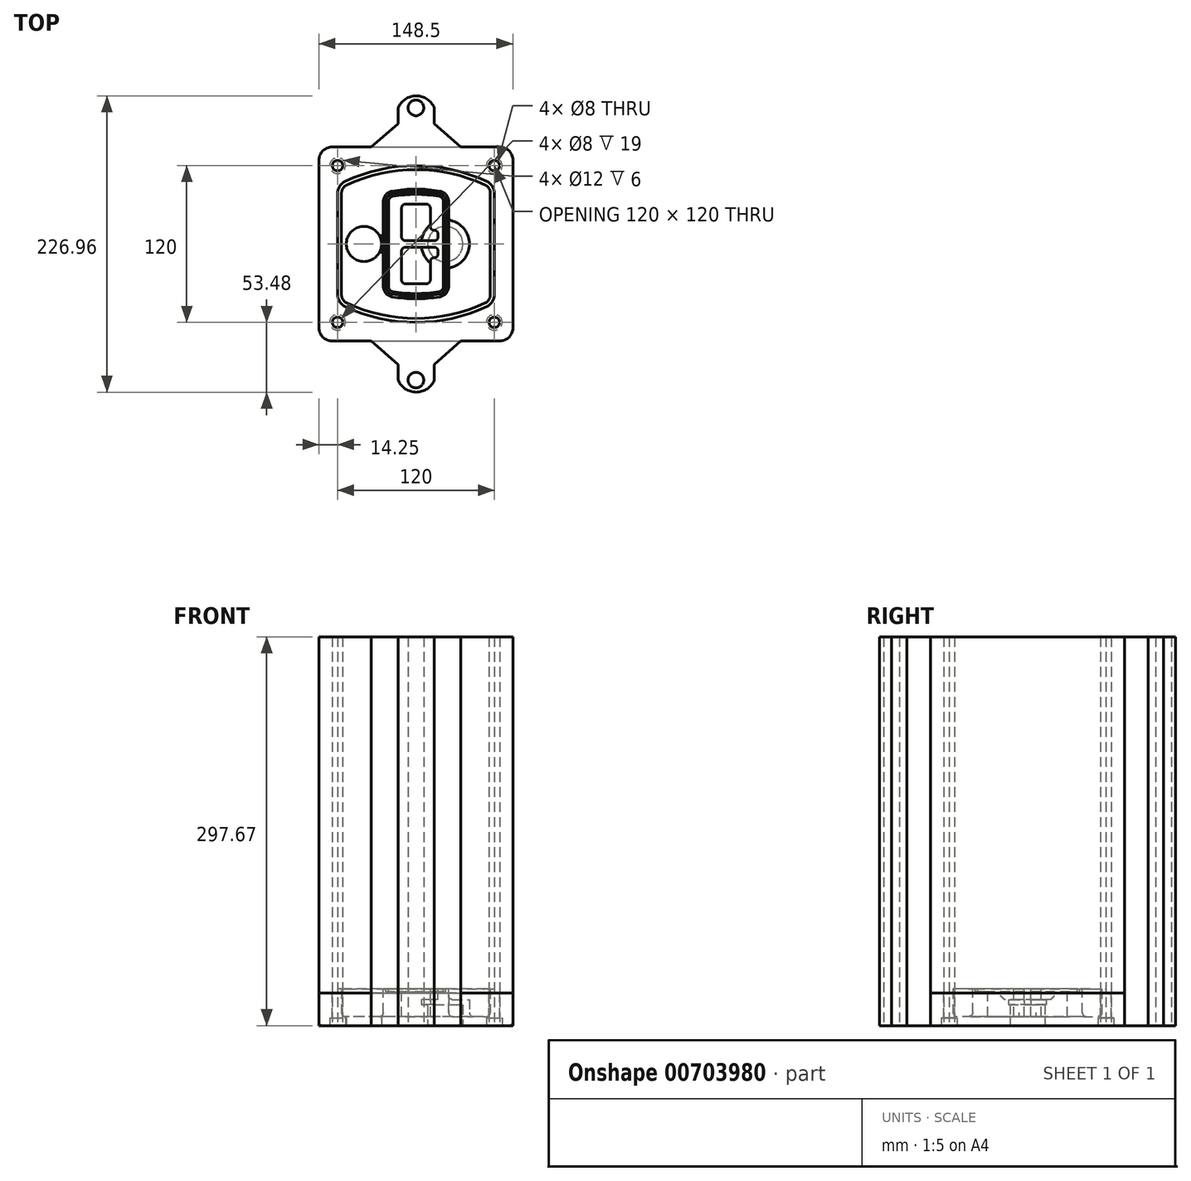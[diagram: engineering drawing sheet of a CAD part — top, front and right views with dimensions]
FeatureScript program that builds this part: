
annotation { "Feature Type Name" : "Feature", "Feature Type Description" : "" }
export const myFeature = defineFeature(function(context is Context, id is Id, definition is map)
    precondition{}
    {
        {
            var Q0;
            Q0=qCreatedBy(makeId("Top.planeOp"),FACE);
            var sketch = newSketch(context, id + "F0", { "sketchPlane" : qUnion([Q0])});
            skPoint(sketch, "E0.rect.middle", {"position": v(0, 0) * mm});
            skLineSegment(sketch, "E1.bottom", {"start": v(-64.25, -74.25) * mm, "end": v(64.25, -74.25) * mm});
            skLineSegment(sketch, "E1.top", {"start": v(-64.25, 74.25) * mm, "end": v(64.25, 74.25) * mm});
            skLineSegment(sketch, "E1.left", {"start": v(-74.25, -64.25) * mm, "end": v(-74.25, 64.25) * mm});
            skLineSegment(sketch, "E1.right", {"start": v(74.25, -64.25) * mm, "end": v(74.25, 64.25) * mm});
            skLineSegment(sketch, "E2", {"start": v(-74.25, 74.25) * mm, "end": v(74.25, -74.25) * mm, "construction": true});
            skLineSegment(sketch, "E3", {"start": v(74.25, 74.25) * mm, "end": v(-74.25, -74.25) * mm, "construction": true});
            skCircle(sketch, "E4", {"center": v(-60, 60) * mm, "radius": 4 * mm});
            skCircle(sketch, "E5", {"center": v(60, 60) * mm, "radius": 4 * mm});
            skCircle(sketch, "E6", {"center": v(60, -60) * mm, "radius": 4 * mm});
            skCircle(sketch, "E7", {"center": v(-60, -60) * mm, "radius": 4 * mm});
            skLineSegment(sketch, "E8", {"start": v(-60, 60) * mm, "end": v(60, 60) * mm, "construction": true});
            skLineSegment(sketch, "E9", {"start": v(60, 60) * mm, "end": v(60, -60) * mm, "construction": true});
            skLineSegment(sketch, "E10", {"start": v(60, -60) * mm, "end": v(-60, -60) * mm, "construction": true});
            skLineSegment(sketch, "E11", {"start": v(-60, -60) * mm, "end": v(-60, 60) * mm, "construction": true});
            skLineSegment(sketch, "E12", {"start": v(-60, 38.83) * mm, "end": v(-60, -38.83) * mm});
            skLineSegment(sketch, "E13", {"start": v(60, 38.83) * mm, "end": v(60, -38.83) * mm});
            skArc(sketch, "E14", {"start": v(54.26, 47.88) * mm, "mid": v(0, 60) * mm, "end": v(-54.26, 47.88) * mm});
            skArc(sketch, "E15", {"start": v(-54.26, -47.88) * mm, "mid": v(0, -60) * mm, "end": v(54.26, -47.88) * mm});
            skLineSegment(sketch, "E16", {"start": v(-60, 0) * mm, "end": v(60, 0) * mm, "construction": true});
            skPoint(sketch, "E17.visualSharp", {"position": v(-60, -45) * mm});
            skArc(sketch, "E17.filletArc", {"start": v(-60, -38.83) * mm, "mid": v(-58.44, -44.2) * mm, "end": v(-54.26, -47.88) * mm});
            skPoint(sketch, "E18.visualSharp", {"position": v(-60, 45) * mm});
            skArc(sketch, "E18.filletArc", {"start": v(-54.26, 47.88) * mm, "mid": v(-58.44, 44.2) * mm, "end": v(-60, 38.83) * mm});
            skPoint(sketch, "E19.visualSharp", {"position": v(60, 45) * mm});
            skArc(sketch, "E19.filletArc", {"start": v(60, 38.83) * mm, "mid": v(58.44, 44.2) * mm, "end": v(54.26, 47.88) * mm});
            skPoint(sketch, "E20.visualSharp", {"position": v(60, -45) * mm});
            skArc(sketch, "E20.filletArc", {"start": v(54.26, -47.88) * mm, "mid": v(58.44, -44.2) * mm, "end": v(60, -38.83) * mm});
            skPoint(sketch, "E21.visualSharp", {"position": v(-74.25, 74.25) * mm});
            skArc(sketch, "E21.filletArc", {"start": v(-64.25, 74.25) * mm, "mid": v(-71.32, 71.32) * mm, "end": v(-74.25, 64.25) * mm});
            skPoint(sketch, "E22.visualSharp", {"position": v(74.25, 74.25) * mm});
            skArc(sketch, "E22.filletArc", {"start": v(74.25, 64.25) * mm, "mid": v(71.32, 71.32) * mm, "end": v(64.25, 74.25) * mm});
            skPoint(sketch, "E23.visualSharp", {"position": v(74.25, -74.25) * mm});
            skArc(sketch, "E23.filletArc", {"start": v(64.25, -74.25) * mm, "mid": v(71.32, -71.32) * mm, "end": v(74.25, -64.25) * mm});
            skPoint(sketch, "E24.visualSharp", {"position": v(-74.25, -74.25) * mm});
            skArc(sketch, "E24.filletArc", {"start": v(-74.25, -64.25) * mm, "mid": v(-71.32, -71.32) * mm, "end": v(-64.25, -74.25) * mm});
            skArc(sketch, "E25.0", {"start": v(57, 38.83) * mm, "mid": v(55.9, 42.58) * mm, "end": v(52.98, 45.17) * mm});
            skLineSegment(sketch, "E25.1", {"start": v(57, 38.83) * mm, "end": v(57, -38.83) * mm});
            skArc(sketch, "E25.2", {"start": v(52.98, -45.17) * mm, "mid": v(55.9, -42.58) * mm, "end": v(57, -38.83) * mm});
            skArc(sketch, "E25.3", {"start": v(-52.98, -45.17) * mm, "mid": v(0, -57) * mm, "end": v(52.98, -45.17) * mm});
            skArc(sketch, "E25.4", {"start": v(-57, -38.83) * mm, "mid": v(-55.9, -42.58) * mm, "end": v(-52.98, -45.17) * mm});
            skArc(sketch, "E25.5", {"start": v(52.98, 45.17) * mm, "mid": v(0, 57) * mm, "end": v(-52.98, 45.17) * mm});
            skLineSegment(sketch, "E25.6", {"start": v(-57, 38.83) * mm, "end": v(-57, -38.83) * mm});
            skArc(sketch, "E25.7", {"start": v(-52.98, 45.17) * mm, "mid": v(-55.9, 42.58) * mm, "end": v(-57, 38.83) * mm});
            skArc(sketch, "E26.0", {"start": v(-55.96, 51.5) * mm, "mid": v(-61.82, 46.33) * mm, "end": v(-64, 38.83) * mm});
            skArc(sketch, "E26.1", {"start": v(55.96, 51.5) * mm, "mid": v(0, 64) * mm, "end": v(-55.96, 51.5) * mm});
            skArc(sketch, "E26.2", {"start": v(64, 38.83) * mm, "mid": v(61.82, 46.33) * mm, "end": v(55.96, 51.5) * mm});
            skLineSegment(sketch, "E26.3", {"start": v(64, 38.83) * mm, "end": v(64, -38.83) * mm});
            skArc(sketch, "E26.4", {"start": v(55.96, -51.5) * mm, "mid": v(61.82, -46.33) * mm, "end": v(64, -38.83) * mm});
            skLineSegment(sketch, "E26.5", {"start": v(-64, 38.83) * mm, "end": v(-64, -38.83) * mm});
            skArc(sketch, "E26.6", {"start": v(-55.96, -51.5) * mm, "mid": v(0, -64) * mm, "end": v(55.96, -51.5) * mm});
            skArc(sketch, "E26.7", {"start": v(-64, -38.83) * mm, "mid": v(-61.82, -46.33) * mm, "end": v(-55.96, -51.5) * mm});
            skSolve(sketch);
        }
        {
            var Q0;
            Q0=makeQuery(id+"F0.imprint","IMPRINT",FACE,{"disambiguationData":[TD([[makeQuery(id+"F0.imprint","IMPRINT",EDGE,{"derivedFrom":sQuery(id+"F0.wireOp",EDGE,"E1.bottom")}),1.0]])]});
            var Q1;
            Q1=makeQuery(id+"F0.imprint","IMPRINT",FACE,{"disambiguationData":[TD([[makeQuery(id+"F0.imprint","IMPRINT",EDGE,{"derivedFrom":sQuery(id+"F0.wireOp",EDGE,"E12")}),1.0]])]});
            var Q2;
            Q2=makeQuery(id+"F0.imprint","IMPRINT",FACE,{"disambiguationData":[TD([[makeQuery(id+"F0.imprint","IMPRINT",EDGE,{"derivedFrom":sQuery(id+"F0.wireOp",EDGE,"E25.0")}),1.0]])]});
            var Q3;
            Q3=makeQuery(id+"F0.imprint","IMPRINT",FACE,{"disambiguationData":[TD([[makeQuery(id+"F0.imprint","IMPRINT",EDGE,{"derivedFrom":sQuery(id+"F0.wireOp",EDGE,"E12")}),-1.0]])]});
            extrude(context, id + "F1", {"entities" : qUnion([Q0, Q1, Q2, Q3]), "oppositeDirection" : true, "depth" : 25 * mm});
        }
        {
            var Q0;
            Q0=makeQuery(id+"F0.imprint","IMPRINT",FACE,{"disambiguationData":[TD([[makeQuery(id+"F0.imprint","IMPRINT",EDGE,{"derivedFrom":sQuery(id+"F0.wireOp",EDGE,"E12")}),1.0]])]});
            extrude(context, id + "F2", {"entities" : qUnion([Q0]), "operationType" : NewBodyOperationType.ADD, "depth" : 3 * mm});
        }
        {
            var Q0;
            Q0=makeQuery(id+"F0.imprint","IMPRINT",FACE,{"disambiguationData":[TD([[makeQuery(id+"F0.imprint","IMPRINT",EDGE,{"derivedFrom":sQuery(id+"F0.wireOp",EDGE,"E25.0")}),1.0]])]});
            extrude(context, id + "F3", {"entities" : qUnion([Q0]), "operationType" : NewBodyOperationType.REMOVE, "oppositeDirection" : true, "depth" : 18 * mm});
        }
        {
            var Q0;
            Q0=makeQuery(id+"F2.opExtrude","CAP_FACE",FACE,{"disambiguationData":[OSD([sQuery(id+"F0.wireOp",EDGE,"E12"),sQuery(id+"F0.wireOp",EDGE,"E13"),sQuery(id+"F0.wireOp",EDGE,"E14"),sQuery(id+"F0.wireOp",EDGE,"E15"),sQuery(id+"F0.wireOp",EDGE,"E17.filletArc"),sQuery(id+"F0.wireOp",EDGE,"E18.filletArc"),sQuery(id+"F0.wireOp",EDGE,"E19.filletArc"),sQuery(id+"F0.wireOp",EDGE,"E20.filletArc"),sQuery(id+"F0.wireOp",EDGE,"E25.0"),sQuery(id+"F0.wireOp",EDGE,"E25.1"),sQuery(id+"F0.wireOp",EDGE,"E25.2"),sQuery(id+"F0.wireOp",EDGE,"E25.3"),sQuery(id+"F0.wireOp",EDGE,"E25.4"),sQuery(id+"F0.wireOp",EDGE,"E25.5"),sQuery(id+"F0.wireOp",EDGE,"E25.6"),sQuery(id+"F0.wireOp",EDGE,"E25.7")])],"isStart":false});
            var sketch = newSketch(context, id + "F4", { "sketchPlane" : qUnion([Q0])});
            skArc(sketch, "E27.0", {"start": v(-18.34, -40.45) * mm, "mid": v(0, -42) * mm, "end": v(18.34, -40.45) * mm});
            skArc(sketch, "E28.0", {"start": v(18.34, 40.45) * mm, "mid": v(0, 42) * mm, "end": v(-18.34, 40.45) * mm});
            skLineSegment(sketch, "E29", {"start": v(-25, 32.57) * mm, "end": v(-25, -32.57) * mm});
            skLineSegment(sketch, "E30", {"start": v(25, 32.57) * mm, "end": v(25, -32.57) * mm});
            skLineSegment(sketch, "E31", {"start": v(-25, 39.1) * mm, "end": v(25, 39.1) * mm, "construction": true});
            skLineSegment(sketch, "E32", {"start": v(-25, -39.1) * mm, "end": v(25, -39.1) * mm, "construction": true});
            skPoint(sketch, "E33.visualSharp", {"position": v(-25, 39.1) * mm});
            skArc(sketch, "E33.filletArc", {"start": v(-18.34, 40.45) * mm, "mid": v(-23.11, 37.73) * mm, "end": v(-25, 32.57) * mm});
            skPoint(sketch, "E34.visualSharp", {"position": v(25, 39.1) * mm});
            skArc(sketch, "E34.filletArc", {"start": v(25, 32.57) * mm, "mid": v(23.11, 37.73) * mm, "end": v(18.34, 40.45) * mm});
            skPoint(sketch, "E35.visualSharp", {"position": v(25, -39.1) * mm});
            skArc(sketch, "E35.filletArc", {"start": v(18.34, -40.45) * mm, "mid": v(23.11, -37.73) * mm, "end": v(25, -32.57) * mm});
            skPoint(sketch, "E36.visualSharp", {"position": v(-25, -39.1) * mm});
            skArc(sketch, "E36.filletArc", {"start": v(-25, -32.57) * mm, "mid": v(-23.11, -37.73) * mm, "end": v(-18.34, -40.45) * mm});
            skArc(sketch, "E37.0", {"start": v(52.98, 45.17) * mm, "mid": v(0, 57) * mm, "end": v(-52.98, 45.17) * mm});
            skArc(sketch, "E37.1", {"start": v(-52.98, 45.17) * mm, "mid": v(-55.9, 42.58) * mm, "end": v(-57, 38.83) * mm});
            skLineSegment(sketch, "E37.2", {"start": v(-57, 38.83) * mm, "end": v(-57, -38.83) * mm});
            skArc(sketch, "E37.3", {"start": v(-57, -38.83) * mm, "mid": v(-55.9, -42.58) * mm, "end": v(-52.98, -45.17) * mm});
            skArc(sketch, "E37.4", {"start": v(-52.98, -45.17) * mm, "mid": v(0, -57) * mm, "end": v(52.98, -45.17) * mm});
            skArc(sketch, "E37.5", {"start": v(52.98, -45.17) * mm, "mid": v(55.9, -42.58) * mm, "end": v(57, -38.83) * mm});
            skLineSegment(sketch, "E37.6", {"start": v(57, 38.83) * mm, "end": v(57, -38.83) * mm});
            skArc(sketch, "E37.7", {"start": v(57, 38.83) * mm, "mid": v(55.9, 42.58) * mm, "end": v(52.98, 45.17) * mm});
            skLineSegment(sketch, "E38.0", {"start": v(23, 32.57) * mm, "end": v(23, -32.57) * mm});
            skArc(sketch, "E38.1", {"start": v(18, -38.48) * mm, "mid": v(21.58, -36.44) * mm, "end": v(23, -32.57) * mm});
            skArc(sketch, "E38.2", {"start": v(-18, -38.48) * mm, "mid": v(0, -40) * mm, "end": v(18, -38.48) * mm});
            skArc(sketch, "E38.3", {"start": v(-23, -32.57) * mm, "mid": v(-21.58, -36.44) * mm, "end": v(-18, -38.48) * mm});
            skLineSegment(sketch, "E38.4", {"start": v(-23, 32.57) * mm, "end": v(-23, -32.57) * mm});
            skArc(sketch, "E38.5", {"start": v(23, 32.57) * mm, "mid": v(21.58, 36.44) * mm, "end": v(18, 38.48) * mm});
            skArc(sketch, "E38.6", {"start": v(-18, 38.48) * mm, "mid": v(-21.58, 36.44) * mm, "end": v(-23, 32.57) * mm});
            skArc(sketch, "E38.7", {"start": v(18, 38.48) * mm, "mid": v(0, 40) * mm, "end": v(-18, 38.48) * mm});
            skArc(sketch, "E39.0", {"start": v(21, 32.57) * mm, "mid": v(20.06, 35.15) * mm, "end": v(17.67, 36.5) * mm});
            skLineSegment(sketch, "E39.1", {"start": v(21, 32.57) * mm, "end": v(21, -32.57) * mm});
            skArc(sketch, "E39.2", {"start": v(17.67, -36.5) * mm, "mid": v(20.06, -35.15) * mm, "end": v(21, -32.57) * mm});
            skArc(sketch, "E39.3", {"start": v(-17.67, -36.5) * mm, "mid": v(0, -38) * mm, "end": v(17.67, -36.5) * mm});
            skArc(sketch, "E39.4", {"start": v(-21, -32.57) * mm, "mid": v(-20.06, -35.15) * mm, "end": v(-17.67, -36.5) * mm});
            skArc(sketch, "E39.5", {"start": v(17.67, 36.5) * mm, "mid": v(0, 38) * mm, "end": v(-17.67, 36.5) * mm});
            skLineSegment(sketch, "E39.6", {"start": v(-21, 32.57) * mm, "end": v(-21, -32.57) * mm});
            skArc(sketch, "E39.7", {"start": v(-17.67, 36.5) * mm, "mid": v(-20.06, 35.15) * mm, "end": v(-21, 32.57) * mm});
            skLineSegment(sketch, "E40", {"start": v(-25, 0) * mm, "end": v(25, 0) * mm, "construction": true});
            skLineSegment(sketch, "E41", {"start": v(-11, 5.5) * mm, "end": v(-11, 27.5) * mm});
            skLineSegment(sketch, "E42", {"start": v(-8, 30.5) * mm, "end": v(8, 30.5) * mm});
            skLineSegment(sketch, "E43", {"start": v(11, 27.5) * mm, "end": v(11, 13.5) * mm});
            skLineSegment(sketch, "E44", {"start": v(14, 10.5) * mm, "end": v(14, 10.5) * mm});
            skLineSegment(sketch, "E45", {"start": v(17, 7.5) * mm, "end": v(17, 5.5) * mm});
            skLineSegment(sketch, "E46", {"start": v(14, 2.5) * mm, "end": v(-8, 2.5) * mm});
            skPoint(sketch, "E47.visualSharp", {"position": v(-11, 30.5) * mm});
            skArc(sketch, "E47.filletArc", {"start": v(-8, 30.5) * mm, "mid": v(-10.12, 29.62) * mm, "end": v(-11, 27.5) * mm});
            skPoint(sketch, "E48.visualSharp", {"position": v(11, 30.5) * mm});
            skArc(sketch, "E48.filletArc", {"start": v(11, 27.5) * mm, "mid": v(10.12, 29.62) * mm, "end": v(8, 30.5) * mm});
            skPoint(sketch, "E49.visualSharp", {"position": v(11, 10.5) * mm});
            skArc(sketch, "E49.filletArc", {"start": v(11, 13.5) * mm, "mid": v(11.88, 11.38) * mm, "end": v(14, 10.5) * mm});
            skPoint(sketch, "E50.visualSharp", {"position": v(17, 10.5) * mm});
            skArc(sketch, "E50.filletArc", {"start": v(17, 7.5) * mm, "mid": v(16.12, 9.62) * mm, "end": v(14, 10.5) * mm});
            skPoint(sketch, "E51.visualSharp", {"position": v(17, 2.5) * mm});
            skArc(sketch, "E51.filletArc", {"start": v(14, 2.5) * mm, "mid": v(16.12, 3.38) * mm, "end": v(17, 5.5) * mm});
            skPoint(sketch, "E52.visualSharp", {"position": v(-11, 2.5) * mm});
            skArc(sketch, "E52.filletArc", {"start": v(-11, 5.5) * mm, "mid": v(-10.12, 3.38) * mm, "end": v(-8, 2.5) * mm});
            skLineSegment(sketch, "E53.0.MirrorCS", {"start": v(14, -2.5) * mm, "end": v(-8, -2.5) * mm});
            skArc(sketch, "E54.0.MirrorCS", {"start": v(-11, -5.5) * mm, "mid": v(-10.12, -3.38) * mm, "end": v(-8, -2.5) * mm});
            skLineSegment(sketch, "E55.0.MirrorCS", {"start": v(-11, -5.5) * mm, "end": v(-11, -27.5) * mm});
            skArc(sketch, "E56.0.MirrorCS", {"start": v(-8, -30.5) * mm, "mid": v(-10.12, -29.62) * mm, "end": v(-11, -27.5) * mm});
            skLineSegment(sketch, "E57.0.MirrorCS", {"start": v(-8, -30.5) * mm, "end": v(8, -30.5) * mm});
            skArc(sketch, "E58.0.MirrorCS", {"start": v(11, -27.5) * mm, "mid": v(10.12, -29.62) * mm, "end": v(8, -30.5) * mm});
            skLineSegment(sketch, "E59.0.MirrorCS", {"start": v(11, -27.5) * mm, "end": v(11, -13.5) * mm});
            skArc(sketch, "E60.0.MirrorCS", {"start": v(11, -13.5) * mm, "mid": v(11.88, -11.38) * mm, "end": v(14, -10.5) * mm});
            skArc(sketch, "E61.0.MirrorCS", {"start": v(17, -7.5) * mm, "mid": v(16.12, -9.62) * mm, "end": v(14, -10.5) * mm});
            skLineSegment(sketch, "E62.0.MirrorCS", {"start": v(17, -7.5) * mm, "end": v(17, -5.5) * mm});
            skArc(sketch, "E63.0.MirrorCS", {"start": v(14, -2.5) * mm, "mid": v(16.12, -3.38) * mm, "end": v(17, -5.5) * mm});
            skSolve(sketch);
        }
        {
            var Q0;
            Q0=makeQuery(id+"F4.imprint","IMPRINT",FACE,{"disambiguationData":[TD([[makeQuery(id+"F4.imprint","IMPRINT",EDGE,{"derivedFrom":sQuery(id+"F4.wireOp",EDGE,"E27.0")}),1.0]])]});
            var Q1;
            Q1=makeQuery(id+"F4.imprint","IMPRINT",FACE,{"disambiguationData":[TD([[makeQuery(id+"F4.imprint","IMPRINT",EDGE,{"derivedFrom":sQuery(id+"F4.wireOp",EDGE,"E38.0")}),-1.0]])]});
            var Q2;
            Q2=makeQuery(id+"F4.imprint","IMPRINT",FACE,{"disambiguationData":[TD([[makeQuery(id+"F4.imprint","IMPRINT",EDGE,{"derivedFrom":sQuery(id+"F4.wireOp",EDGE,"E39.0")}),1.0]])]});
            extrude(context, id + "F5", {"entities" : qUnion([Q0, Q1, Q2]), "operationType" : NewBodyOperationType.ADD, "endBound" : BoundingType.UP_TO_NEXT, "oppositeDirection" : true, "depth" : 25 * mm});
        }
        {
            var Q0;
            Q0=makeQuery(id+"F4.imprint","IMPRINT",FACE,{"disambiguationData":[TD([[makeQuery(id+"F4.imprint","IMPRINT",EDGE,{"derivedFrom":sQuery(id+"F4.wireOp",EDGE,"E38.0")}),-1.0]])]});
            extrude(context, id + "F6", {"entities" : qUnion([Q0]), "operationType" : NewBodyOperationType.REMOVE, "oppositeDirection" : true, "depth" : 2 * mm});
        }
        {
            var Q0;
            Q0=makeQuery(id+"F1.opExtrude","CAP_FACE",FACE,{"disambiguationData":[OSD([sQuery(id+"F0.wireOp",EDGE,"E1.bottom"),sQuery(id+"F0.wireOp",EDGE,"E1.top"),sQuery(id+"F0.wireOp",EDGE,"E1.left"),sQuery(id+"F0.wireOp",EDGE,"E1.right"),sQuery(id+"F0.wireOp",EDGE,"E4"),sQuery(id+"F0.wireOp",EDGE,"E5"),sQuery(id+"F0.wireOp",EDGE,"E6"),sQuery(id+"F0.wireOp",EDGE,"E7"),sQuery(id+"F0.wireOp",EDGE,"E21.filletArc"),sQuery(id+"F0.wireOp",EDGE,"E22.filletArc"),sQuery(id+"F0.wireOp",EDGE,"E23.filletArc"),sQuery(id+"F0.wireOp",EDGE,"E24.filletArc")])],"isStart":false});
            var sketch = newSketch(context, id + "F7", { "sketchPlane" : qUnion([Q0])});
            skCircle(sketch, "E64", {"center": v(22.5, 0) * mm, "radius": 13.47 * mm});
            skCircle(sketch, "E65", {"center": v(-39.81, 0) * mm, "radius": 13.47 * mm});
            skLineSegment(sketch, "E66", {"start": v(74.25, 0) * mm, "end": v(-74.25, 0) * mm});
            skCircle(sketch, "E67", {"center": v(22.5, 0) * mm, "radius": 18.47 * mm});
            skCircle(sketch, "E68", {"center": v(60, -60) * mm, "radius": 6 * mm});
            skCircle(sketch, "E69", {"center": v(-60, -60) * mm, "radius": 6 * mm});
            skCircle(sketch, "E70", {"center": v(-60, 60) * mm, "radius": 6 * mm});
            skCircle(sketch, "E71", {"center": v(60, 60) * mm, "radius": 6 * mm});
            skSolve(sketch);
        }
        {
            var Q0;
            {var subQ1=sQuery(id+"F7.wireOp",EDGE,"E66");var subQ4=sQuery(id+"F7.wireOp",EDGE,"E64");var subQ6=makeQuery(id+"F7.imprint","INTERSECT",VERTEX,{"disambiguationData":[OD(0.0)],"derivedFrom":[subQ4,subQ1]});Q0=makeQuery(id+"F7.imprint","IMPRINT",FACE,{"disambiguationData":[TD([[makeQuery(id+"F7.imprint","IMPRINT",EDGE,{"disambiguationData":[TD([[subQ6,-1.0]])],"derivedFrom":subQ4}),-1.0]])]});}
            var Q1;
            {var subQ0=sQuery(id+"F7.wireOp",EDGE,"E66");var subQ1=sQuery(id+"F7.wireOp",EDGE,"E64");var subQ3=makeQuery(id+"F7.imprint","INTERSECT",VERTEX,{"disambiguationData":[OD(0.0)],"derivedFrom":[subQ1,subQ0]});Q1=makeQuery(id+"F7.imprint","IMPRINT",FACE,{"disambiguationData":[TD([[makeQuery(id+"F7.imprint","IMPRINT",EDGE,{"disambiguationData":[TD([[subQ3,-1.0]])],"derivedFrom":subQ1}),1.0]])]});}
            var Q2;
            {var subQ0=sQuery(id+"F7.wireOp",EDGE,"E66");var subQ1=sQuery(id+"F7.wireOp",EDGE,"E64");var subQ3=makeQuery(id+"F7.imprint","INTERSECT",VERTEX,{"disambiguationData":[OD(0.0)],"derivedFrom":[subQ1,subQ0]});Q2=makeQuery(id+"F7.imprint","IMPRINT",FACE,{"disambiguationData":[TD([[makeQuery(id+"F7.imprint","IMPRINT",EDGE,{"disambiguationData":[TD([[subQ3,1.0]])],"derivedFrom":subQ1}),1.0]])]});}
            var Q3;
            {var subQ1=sQuery(id+"F7.wireOp",EDGE,"E66");var subQ4=sQuery(id+"F7.wireOp",EDGE,"E64");var subQ6=makeQuery(id+"F7.imprint","INTERSECT",VERTEX,{"disambiguationData":[OD(0.0)],"derivedFrom":[subQ4,subQ1]});Q3=makeQuery(id+"F7.imprint","IMPRINT",FACE,{"disambiguationData":[TD([[makeQuery(id+"F7.imprint","IMPRINT",EDGE,{"disambiguationData":[TD([[subQ6,1.0]])],"derivedFrom":subQ4}),-1.0]])]});}
            extrude(context, id + "F8", {"entities" : qUnion([Q0, Q1, Q2, Q3]), "operationType" : NewBodyOperationType.ADD, "oppositeDirection" : true, "depth" : 20 * mm});
        }
        {
            var Q0;
            {var subQ0=sQuery(id+"F7.wireOp",EDGE,"E66");var subQ1=sQuery(id+"F7.wireOp",EDGE,"E64");var subQ3=makeQuery(id+"F7.imprint","INTERSECT",VERTEX,{"disambiguationData":[OD(0.0)],"derivedFrom":[subQ1,subQ0]});Q0=makeQuery(id+"F7.imprint","IMPRINT",FACE,{"disambiguationData":[TD([[makeQuery(id+"F7.imprint","IMPRINT",EDGE,{"disambiguationData":[TD([[subQ3,-1.0]])],"derivedFrom":subQ1}),1.0]])]});}
            var Q1;
            {var subQ0=sQuery(id+"F7.wireOp",EDGE,"E66");var subQ1=sQuery(id+"F7.wireOp",EDGE,"E64");var subQ3=makeQuery(id+"F7.imprint","INTERSECT",VERTEX,{"disambiguationData":[OD(0.0)],"derivedFrom":[subQ1,subQ0]});Q1=makeQuery(id+"F7.imprint","IMPRINT",FACE,{"disambiguationData":[TD([[makeQuery(id+"F7.imprint","IMPRINT",EDGE,{"disambiguationData":[TD([[subQ3,1.0]])],"derivedFrom":subQ1}),1.0]])]});}
            extrude(context, id + "F9", {"entities" : qUnion([Q0, Q1]), "operationType" : NewBodyOperationType.REMOVE, "oppositeDirection" : true, "depth" : 16 * mm});
        }
        {
            var Q0;
            {var subQ0=sQuery(id+"F7.wireOp",EDGE,"E66");var subQ1=sQuery(id+"F7.wireOp",EDGE,"E65");var subQ3=makeQuery(id+"F7.imprint","INTERSECT",VERTEX,{"disambiguationData":[OD(0.0)],"derivedFrom":[subQ1,subQ0]});Q0=makeQuery(id+"F7.imprint","IMPRINT",FACE,{"disambiguationData":[TD([[makeQuery(id+"F7.imprint","IMPRINT",EDGE,{"disambiguationData":[TD([[subQ3,-1.0]])],"derivedFrom":subQ1}),1.0]])]});}
            var Q1;
            {var subQ0=sQuery(id+"F7.wireOp",EDGE,"E66");var subQ1=sQuery(id+"F7.wireOp",EDGE,"E65");var subQ3=makeQuery(id+"F7.imprint","INTERSECT",VERTEX,{"disambiguationData":[OD(0.0)],"derivedFrom":[subQ1,subQ0]});Q1=makeQuery(id+"F7.imprint","IMPRINT",FACE,{"disambiguationData":[TD([[makeQuery(id+"F7.imprint","IMPRINT",EDGE,{"disambiguationData":[TD([[subQ3,1.0]])],"derivedFrom":subQ1}),1.0]])]});}
            extrude(context, id + "F10", {"entities" : qUnion([Q0, Q1]), "operationType" : NewBodyOperationType.REMOVE, "oppositeDirection" : true, "depth" : 25 * mm});
        }
        {
            var Q0;
            Q0=makeQuery(id+"F7.imprint","IMPRINT",FACE,{"disambiguationData":[TD([[makeQuery(id+"F7.imprint","IMPRINT",EDGE,{"derivedFrom":sQuery(id+"F7.wireOp",EDGE,"E68")}),1.0]])]});
            var Q1;
            Q1=makeQuery(id+"F7.imprint","IMPRINT",FACE,{"disambiguationData":[TD([[makeQuery(id+"F7.imprint","IMPRINT",EDGE,{"derivedFrom":makeQuery(id+"F1.opExtrude","CAP_EDGE",EDGE,{"disambiguationData":[OSD([sQuery(id+"F0.wireOp",EDGE,"E5")])],"isStart":false})}),-1.0]])]});
            var Q2;
            Q2=makeQuery(id+"F7.imprint","IMPRINT",FACE,{"disambiguationData":[TD([[makeQuery(id+"F7.imprint","IMPRINT",EDGE,{"derivedFrom":sQuery(id+"F7.wireOp",EDGE,"E69")}),1.0]])]});
            var Q3;
            Q3=makeQuery(id+"F7.imprint","IMPRINT",FACE,{"disambiguationData":[TD([[makeQuery(id+"F7.imprint","IMPRINT",EDGE,{"derivedFrom":makeQuery(id+"F1.opExtrude","CAP_EDGE",EDGE,{"disambiguationData":[OSD([sQuery(id+"F0.wireOp",EDGE,"E4")])],"isStart":false})}),-1.0]])]});
            var Q4;
            Q4=makeQuery(id+"F7.imprint","IMPRINT",FACE,{"disambiguationData":[TD([[makeQuery(id+"F7.imprint","IMPRINT",EDGE,{"derivedFrom":sQuery(id+"F7.wireOp",EDGE,"E70")}),1.0]])]});
            var Q5;
            Q5=makeQuery(id+"F7.imprint","IMPRINT",FACE,{"disambiguationData":[TD([[makeQuery(id+"F7.imprint","IMPRINT",EDGE,{"derivedFrom":makeQuery(id+"F1.opExtrude","CAP_EDGE",EDGE,{"disambiguationData":[OSD([sQuery(id+"F0.wireOp",EDGE,"E7")])],"isStart":false})}),-1.0]])]});
            var Q6;
            Q6=makeQuery(id+"F7.imprint","IMPRINT",FACE,{"disambiguationData":[TD([[makeQuery(id+"F7.imprint","IMPRINT",EDGE,{"derivedFrom":sQuery(id+"F7.wireOp",EDGE,"E71")}),1.0]])]});
            var Q7;
            Q7=makeQuery(id+"F7.imprint","IMPRINT",FACE,{"disambiguationData":[TD([[makeQuery(id+"F7.imprint","IMPRINT",EDGE,{"derivedFrom":makeQuery(id+"F1.opExtrude","CAP_EDGE",EDGE,{"disambiguationData":[OSD([sQuery(id+"F0.wireOp",EDGE,"E6")])],"isStart":false})}),-1.0]])]});
            extrude(context, id + "F11", {"entities" : qUnion([Q0, Q1, Q2, Q3, Q4, Q5, Q6, Q7]), "operationType" : NewBodyOperationType.REMOVE, "oppositeDirection" : true, "depth" : 6 * mm});
        }
        {
            var Q0;
            Q0=makeQuery(id+"F9.boolean.opBoolean","COPY",FACE,{"derivedFrom":makeQuery(id+"F9.opExtrude","CAP_FACE",FACE,{"disambiguationData":[OSD([sQuery(id+"F7.wireOp",EDGE,"E64")])],"isStart":false})});
            var sketch = newSketch(context, id + "F12", { "sketchPlane" : qUnion([Q0])});
            skArc(sketch, "E72.0", {"start": v(11, 14.45) * mm, "mid": v(6.45, 9.13) * mm, "end": v(4.2, 2.5) * mm});
            skArc(sketch, "E72.1", {"start": v(4.2, -2.5) * mm, "mid": v(6.45, -9.13) * mm, "end": v(11, -14.45) * mm});
            skLineSegment(sketch, "E73", {"start": v(4.2, -2.5) * mm, "end": v(14, -2.5) * mm});
            skLineSegment(sketch, "E74.0", {"start": v(14, 2.5) * mm, "end": v(4.2, 2.5) * mm});
            skArc(sketch, "E74.1", {"start": v(14, 2.5) * mm, "mid": v(16.12, 3.38) * mm, "end": v(17, 5.5) * mm});
            skLineSegment(sketch, "E74.2", {"start": v(17, 7.5) * mm, "end": v(17, 5.5) * mm});
            skArc(sketch, "E74.3", {"start": v(17, 7.5) * mm, "mid": v(16.12, 9.62) * mm, "end": v(14, 10.5) * mm});
            skArc(sketch, "E74.4", {"start": v(11, 13.5) * mm, "mid": v(11.88, 11.38) * mm, "end": v(14, 10.5) * mm});
            skLineSegment(sketch, "E74.5", {"start": v(11, 14.45) * mm, "end": v(11, 13.5) * mm});
            skLineSegment(sketch, "E74.7", {"start": v(14, -2.5) * mm, "end": v(4.2, -2.5) * mm});
            skArc(sketch, "E74.8", {"start": v(14, -2.5) * mm, "mid": v(16.12, -3.38) * mm, "end": v(17, -5.5) * mm});
            skLineSegment(sketch, "E74.9", {"start": v(17, -7.5) * mm, "end": v(17, -5.5) * mm});
            skArc(sketch, "E74.10", {"start": v(17, -7.5) * mm, "mid": v(16.12, -9.62) * mm, "end": v(14, -10.5) * mm});
            skArc(sketch, "E74.11", {"start": v(11, -13.5) * mm, "mid": v(11.88, -11.38) * mm, "end": v(14, -10.5) * mm});
            skLineSegment(sketch, "E74.12", {"start": v(11, -14.45) * mm, "end": v(11, -13.5) * mm});
            skPoint(sketch, "E75.orphan", {"position": v(11, -27.5) * mm});
            skPoint(sketch, "E76.orphan", {"position": v(-8, -2.5) * mm});
            skPoint(sketch, "E77.orphan", {"position": v(-8, 2.5) * mm});
            skPoint(sketch, "E78.orphan", {"position": v(11, 27.5) * mm});
            skSolve(sketch);
        }
        {
            var Q0;
            {var subQ7=sQuery(id+"F12.wireOp",EDGE,"E72.0");var subQ14=sQuery(id+"F12.wireOp",EDGE,"E72.1");var subQ16=sQuery(id+"F12.wireOp",EDGE,"E74.1");var subQ18=sQuery(id+"F12.wireOp",EDGE,"E74.8");Q0=qUnion([makeQuery(id+"F12.imprint","IMPRINT",FACE,{"disambiguationData":[TD([[makeQuery(id+"F12.imprint","IMPRINT",EDGE,{"derivedFrom":subQ7}),1.0]])]}),makeQuery(id+"F12.imprint","IMPRINT",FACE,{"disambiguationData":[TD([[makeQuery(id+"F12.imprint","IMPRINT",EDGE,{"derivedFrom":subQ14}),1.0]])]}),makeQuery(id+"F12.imprint","IMPRINT",FACE,{"disambiguationData":[TD([[makeQuery(id+"F12.imprint","IMPRINT",EDGE,{"derivedFrom":subQ16}),1.0]])]}),makeQuery(id+"F12.imprint","IMPRINT",FACE,{"disambiguationData":[TD([[makeQuery(id+"F12.imprint","IMPRINT",EDGE,{"derivedFrom":subQ18}),-1.0]])]})]);}
            var Q1;
            Q1=makeQuery(id+"F5.boolean.opBoolean","SPLIT",FACE,{"disambiguationData":[TD([makeQuery(id+"F5.opExtrude","SWEPT_FACE",FACE,{"disambiguationData":[OSD([sQuery(id+"F4.wireOp",EDGE,"E41")])]})])],"derivedFrom":makeQuery(id+"F3.boolean.opBoolean","COPY",FACE,{"derivedFrom":makeQuery(id+"F3.opExtrude","CAP_FACE",FACE,{"disambiguationData":[OSD([sQuery(id+"F0.wireOp",EDGE,"E25.0"),sQuery(id+"F0.wireOp",EDGE,"E25.1"),sQuery(id+"F0.wireOp",EDGE,"E25.2"),sQuery(id+"F0.wireOp",EDGE,"E25.3"),sQuery(id+"F0.wireOp",EDGE,"E25.4"),sQuery(id+"F0.wireOp",EDGE,"E25.5"),sQuery(id+"F0.wireOp",EDGE,"E25.6"),sQuery(id+"F0.wireOp",EDGE,"E25.7")])],"isStart":false})})});
            extrude(context, id + "F13", {"entities" : qUnion([Q0]), "operationType" : NewBodyOperationType.REMOVE, "endBound" : BoundingType.UP_TO_SURFACE, "endBoundEntityFace" : qUnion([Q1]), "depth" : 25 * mm});
        }
        {
            var Q0;
            Q0=makeQuery(id+"F3.boolean.opBoolean","COPY",EDGE,{"derivedFrom":makeQuery(id+"F3.opExtrude","CAP_EDGE",EDGE,{"disambiguationData":[OSD([sQuery(id+"F0.wireOp",EDGE,"E25.6")])],"isStart":false})});
            var Q1;
            Q1=makeQuery(id+"F8.boolean.opBoolean","INTERSECT",EDGE,{"derivedFrom":[makeQuery(id+"F5.opExtrude","SWEPT_FACE",FACE,{"disambiguationData":[OSD([sQuery(id+"F4.wireOp",EDGE,"E30")])]}),makeQuery(id+"F8.opExtrude","CAP_FACE",FACE,{"disambiguationData":[OSD([sQuery(id+"F7.wireOp",EDGE,"E67")])],"isStart":false})]});
            var Q2;
            Q2=makeQuery(id+"F8.boolean.opBoolean","INTERSECT",EDGE,{"disambiguationData":[OD(1.0)],"derivedFrom":[makeQuery(id+"F5.opExtrude","SWEPT_FACE",FACE,{"disambiguationData":[OSD([sQuery(id+"F4.wireOp",EDGE,"E30")])]}),makeQuery(id+"F8.opExtrude","SWEPT_FACE",FACE,{"disambiguationData":[OSD([sQuery(id+"F7.wireOp",EDGE,"E67")])]})]});
            var Q3;
            {var subQ0=sQuery(id+"F4.wireOp",EDGE,"E30");Q3=makeQuery(id+"F8.boolean.opBoolean","SPLIT",EDGE,{"disambiguationData":[TD([makeQuery(id+"F5.opExtrude","SWEPT_FACE",FACE,{"disambiguationData":[OSD([sQuery(id+"F4.wireOp",EDGE,"E35.filletArc")])]})])],"derivedFrom":makeQuery(id+"F5.opExtrude","CAP_EDGE",EDGE,{"disambiguationData":[OSD([subQ0])],"isStart":false})});}
            var Q4;
            {var subQ0=sQuery(id+"F0.wireOp",EDGE,"E25.7");var subQ1=sQuery(id+"F0.wireOp",EDGE,"E25.1");var subQ2=sQuery(id+"F0.wireOp",EDGE,"E25.6");var subQ3=sQuery(id+"F0.wireOp",EDGE,"E25.5");var subQ4=sQuery(id+"F0.wireOp",EDGE,"E25.4");var subQ5=sQuery(id+"F0.wireOp",EDGE,"E25.0");var subQ6=sQuery(id+"F0.wireOp",EDGE,"E25.2");var subQ7=sQuery(id+"F0.wireOp",EDGE,"E25.3");Q4=makeQuery(id+"F8.boolean.opBoolean","INTERSECT",EDGE,{"derivedFrom":[makeQuery(id+"F5.boolean.opBoolean","SPLIT",FACE,{"disambiguationData":[TD([makeQuery(id+"F2.opExtrude","SWEPT_FACE",FACE,{"disambiguationData":[OSD([subQ5])]})])],"derivedFrom":makeQuery(id+"F3.boolean.opBoolean","COPY",FACE,{"derivedFrom":makeQuery(id+"F3.opExtrude","CAP_FACE",FACE,{"disambiguationData":[OSD([subQ5,subQ1,subQ6,subQ7,subQ4,subQ3,subQ2,subQ0])],"isStart":false})})}),makeQuery(id+"F8.opExtrude","SWEPT_FACE",FACE,{"disambiguationData":[OSD([sQuery(id+"F7.wireOp",EDGE,"E67")])]})]});}
            var Q5;
            Q5=makeQuery(id+"F8.boolean.opBoolean","INTERSECT",EDGE,{"disambiguationData":[OD(0.0)],"derivedFrom":[makeQuery(id+"F5.opExtrude","SWEPT_FACE",FACE,{"disambiguationData":[OSD([sQuery(id+"F4.wireOp",EDGE,"E30")])]}),makeQuery(id+"F8.opExtrude","SWEPT_FACE",FACE,{"disambiguationData":[OSD([sQuery(id+"F7.wireOp",EDGE,"E67")])]})]});
            fillet(context, id + "F14", {"entities" : qUnion([Q0, Q1, Q2, Q3, Q4, Q5]), "radius" : 3 * mm, "tangentPropagation" : true, "allowEdgeOverflow" : false});
        }
        {
            var Q0;
            Q0=makeQuery(id+"F1.opExtrude","CAP_EDGE",EDGE,{"disambiguationData":[OSD([sQuery(id+"F0.wireOp",EDGE,"E1.bottom")])],"isStart":false});
            fillet(context, id + "F15", {"entities" : qUnion([Q0]), "radius" : 2 * mm, "tangentPropagation" : true, "allowEdgeOverflow" : false});
        }
        {
            var Q0;
            {var subQ0=sQuery(id+"F0.wireOp",EDGE,"E21.filletArc");var subQ1=sQuery(id+"F0.wireOp",EDGE,"E7");var subQ2=sQuery(id+"F0.wireOp",EDGE,"E6");var subQ3=sQuery(id+"F0.wireOp",EDGE,"E5");var subQ4=sQuery(id+"F0.wireOp",EDGE,"E4");var subQ5=sQuery(id+"F0.wireOp",EDGE,"E22.filletArc");var subQ6=sQuery(id+"F0.wireOp",EDGE,"E1.bottom");var subQ7=sQuery(id+"F0.wireOp",EDGE,"E1.right");var subQ8=sQuery(id+"F0.wireOp",EDGE,"E1.top");var subQ9=sQuery(id+"F0.wireOp",EDGE,"E1.left");var subQ10=sQuery(id+"F0.wireOp",EDGE,"E23.filletArc");var subQ11=sQuery(id+"F0.wireOp",EDGE,"E24.filletArc");Q0=makeQuery(id+"F2.boolean.opBoolean","SPLIT",FACE,{"disambiguationData":[TD([makeQuery(id+"F1.opExtrude","SWEPT_FACE",FACE,{"disambiguationData":[OSD([subQ6])]})])],"derivedFrom":makeQuery(id+"F1.opExtrude","CAP_FACE",FACE,{"disambiguationData":[OSD([subQ6,subQ8,subQ9,subQ7,subQ4,subQ3,subQ2,subQ1,subQ0,subQ5,subQ10,subQ11])],"isStart":true})});}
            var sketch = newSketch(context, id + "F16", { "sketchPlane" : qUnion([Q0])});
            skPoint(sketch, "E79", {"position": v(0, 74.25) * mm});
            skLineSegment(sketch, "E80", {"start": v(0, 74.25) * mm, "end": v(0, 104.25) * mm, "construction": true});
            skCircle(sketch, "E81", {"center": v(0, 104.25) * mm, "radius": 6 * mm});
            skLineSegment(sketch, "E82", {"start": v(-64.25, 74.25) * mm, "end": v(-34.25, 74.25) * mm});
            skArc(sketch, "E83", {"start": v(14.08, 104.25) * mm, "mid": v(0.24, 113.48) * mm, "end": v(-13.6, 104.25) * mm});
            skLineSegment(sketch, "E84", {"start": v(-13.6, 104.25) * mm, "end": v(-13.6, 92.25) * mm});
            skLineSegment(sketch, "E85", {"start": v(14.08, 104.25) * mm, "end": v(14.08, 92.25) * mm});
            skLineSegment(sketch, "E86", {"start": v(-13.6, 92.25) * mm, "end": v(-34.25, 74.25) * mm});
            skLineSegment(sketch, "E87", {"start": v(64.25, 74.25) * mm, "end": v(34.25, 74.25) * mm});
            skLineSegment(sketch, "E88", {"start": v(34.25, 74.25) * mm, "end": v(14.08, 92.25) * mm});
            skLineSegment(sketch, "E89", {"start": v(-74.25, 0) * mm, "end": v(74.25, 0) * mm});
            skLineSegment(sketch, "E90.MirrorCS", {"start": v(14.08, -104.25) * mm, "end": v(14.08, -92.25) * mm});
            skLineSegment(sketch, "E91.MirrorCS", {"start": v(-13.6, -104.25) * mm, "end": v(-13.6, -92.25) * mm});
            skPoint(sketch, "E92.MirrorP", {"position": v(0, -74.25) * mm});
            skLineSegment(sketch, "E93.MirrorCS", {"start": v(34.25, -74.25) * mm, "end": v(14.08, -92.25) * mm});
            skLineSegment(sketch, "E94.MirrorCS", {"start": v(64.25, -74.25) * mm, "end": v(34.25, -74.25) * mm});
            skLineSegment(sketch, "E95.MirrorCS", {"start": v(-13.6, -92.25) * mm, "end": v(-34.25, -74.25) * mm});
            skArc(sketch, "E96.MirrorCS", {"start": v(14.08, -104.25) * mm, "mid": v(0.24, -113.48) * mm, "end": v(-13.6, -104.25) * mm});
            skLineSegment(sketch, "E97.MirrorCS", {"start": v(-64.25, -74.25) * mm, "end": v(-34.25, -74.25) * mm});
            skCircle(sketch, "E98.MirrorC", {"center": v(0, -104.25) * mm, "radius": 6 * mm});
            skLineSegment(sketch, "E99.MirrorCS", {"start": v(0, -74.25) * mm, "end": v(0, -104.25) * mm, "construction": true});
            skSolve(sketch);
        }
        {
            var Q0;
            Q0=makeQuery(id+"F16.imprint","IMPRINT",FACE,{"disambiguationData":[TD([[makeQuery(id+"F16.imprint","IMPRINT",EDGE,{"derivedFrom":sQuery(id+"F16.wireOp",EDGE,"E81")}),-1.0]])]});
            var Q1;
            {var subQ3=sQuery(id+"F16.wireOp",EDGE,"E82");Q1=makeQuery(id+"F16.imprint","IMPRINT",FACE,{"disambiguationData":[TD([[makeQuery(id+"F16.imprint","IMPRINT",EDGE,{"derivedFrom":subQ3}),-1.0]])]});}
            var Q2;
            {var subQ1=sQuery(id+"F16.wireOp",EDGE,"E94.MirrorCS");Q2=makeQuery(id+"F16.imprint","IMPRINT",FACE,{"disambiguationData":[TD([[makeQuery(id+"F16.imprint","IMPRINT",EDGE,{"derivedFrom":subQ1}),1.0]])]});}
            var Q3;
            Q3=makeQuery(id+"F16.imprint","IMPRINT",FACE,{"disambiguationData":[TD([[makeQuery(id+"F16.imprint","IMPRINT",EDGE,{"derivedFrom":sQuery(id+"F16.wireOp",EDGE,"E90.MirrorCS")}),1.0]])]});
            extrude(context, id + "F17", {"entities" : qUnion([Q0, Q1, Q2, Q3]), "endBound" : BoundingType.THROUGH_ALL, "depth" : 25 * mm, "offsetDistance" : 25 * mm, "hasSecondDirection" : true, "secondDirectionOppositeDirection" : true, "secondDirectionDepth" : 25 * mm});
        }
    });
